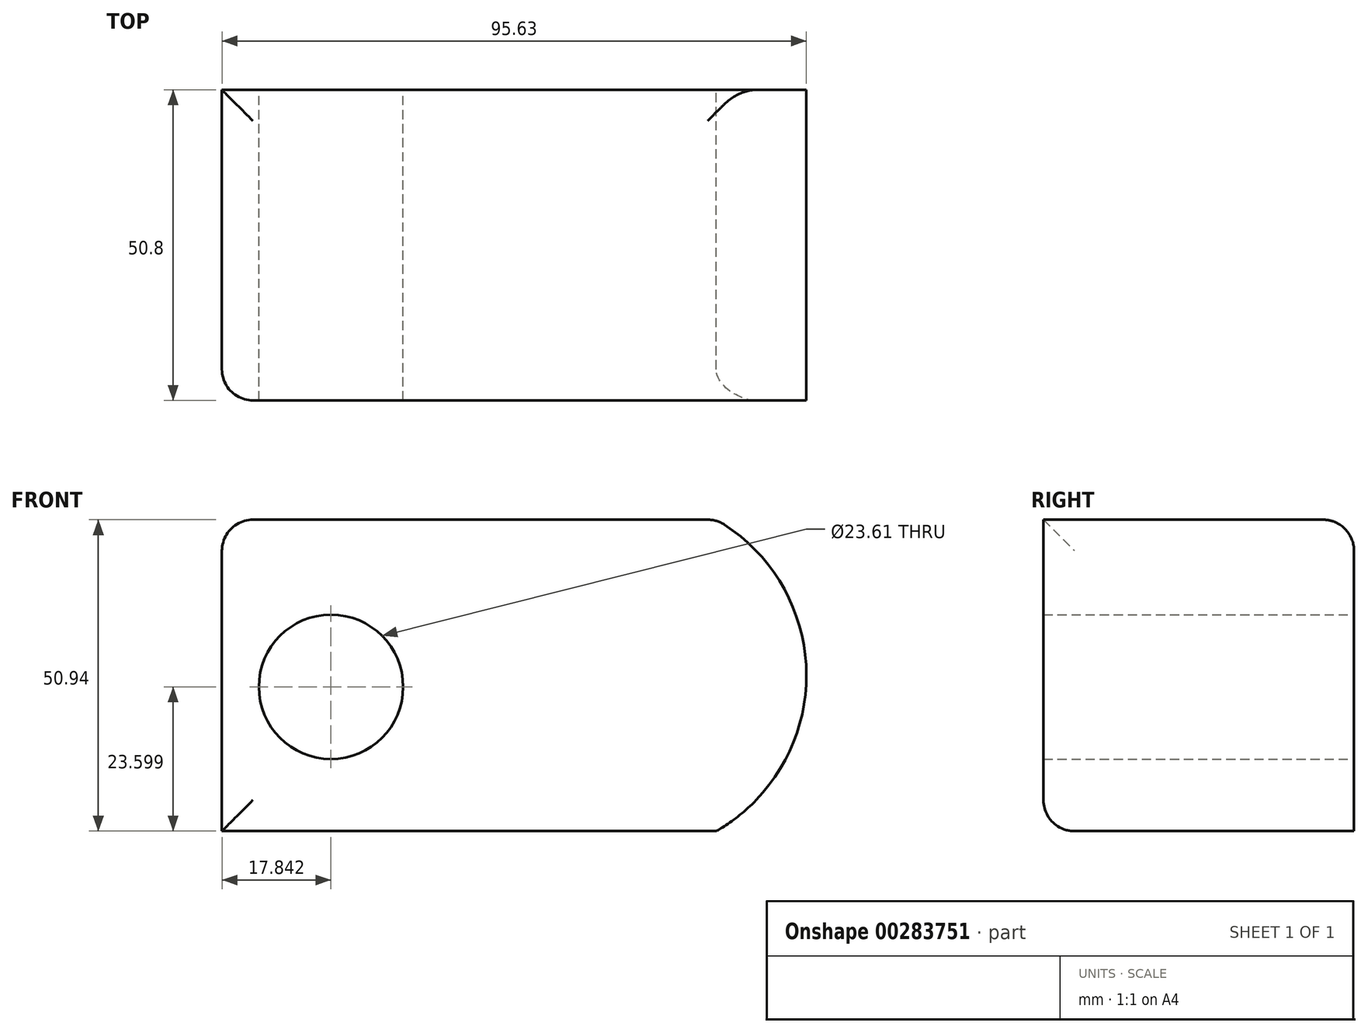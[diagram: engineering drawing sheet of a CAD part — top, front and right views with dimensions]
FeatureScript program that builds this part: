
annotation { "Feature Type Name" : "Feature", "Feature Type Description" : "" }
export const myFeature = defineFeature(function(context is Context, id is Id, definition is map)
    precondition{}
    {
        {
            var Q0;
            Q0=qCreatedBy(makeId("Front.planeOp"),FACE);
            var sketch = newSketch(context, id + "F0", { "sketchPlane" : qUnion([Q0])});
            skLineSegment(sketch, "E0", {"start": v(-56.12, 23.6) * mm, "end": v(24.75, 23.6) * mm});
            skLineSegment(sketch, "E1", {"start": v(-56.12, 23.6) * mm, "end": v(-56.12, -27.34) * mm});
            skLineSegment(sketch, "E2", {"start": v(-56.12, -27.34) * mm, "end": v(24.75, -27.34) * mm});
            skArc(sketch, "E3", {"start": v(24.75, -27.34) * mm, "mid": v(39.5, -1.87) * mm, "end": v(24.75, 23.6) * mm});
            skCircle(sketch, "E4", {"center": v(-38.28, -3.74) * mm, "radius": 11.8 * mm});
            skSolve(sketch);
        }
        {
            var Q0;
            Q0 = qSketchRegion(id + "F0", true);
            extrude(context, id + "F1", {"entities" : qUnion([Q0]), "depth" : 50.8 * mm});
        }
        {
            var Q0;
            Q0=makeQuery(id+"F1.opExtrude","SWEPT_EDGE",EDGE,{"disambiguationData":[OSD([sQuery(id+"F0.wireOp",EDGE,"E0"),sQuery(id+"F0.wireOp",EDGE,"E3")])]});
            var Q1;
            Q1=makeQuery(id+"F1.opExtrude","CAP_EDGE",EDGE,{"disambiguationData":[OSD([sQuery(id+"F0.wireOp",EDGE,"E0")])],"isStart":true});
            var Q2;
            Q2=makeQuery(id+"F1.opExtrude","SWEPT_EDGE",EDGE,{"disambiguationData":[OSD([sQuery(id+"F0.wireOp",EDGE,"E0"),sQuery(id+"F0.wireOp",EDGE,"E1")])]});
            var Q3;
            Q3=makeQuery(id+"F1.opExtrude","CAP_EDGE",EDGE,{"disambiguationData":[OSD([sQuery(id+"F0.wireOp",EDGE,"E1")])],"isStart":false});
            var Q4;
            Q4=makeQuery(id+"F1.opExtrude","CAP_EDGE",EDGE,{"disambiguationData":[OSD([sQuery(id+"F0.wireOp",EDGE,"E2")])],"isStart":false});
            fillet(context, id + "F2", {"entities" : qUnion([Q0, Q1, Q2, Q3, Q4]), "radius" : 5.08 * mm, "tangentPropagation" : true, "allowEdgeOverflow" : false});
        }
    });
